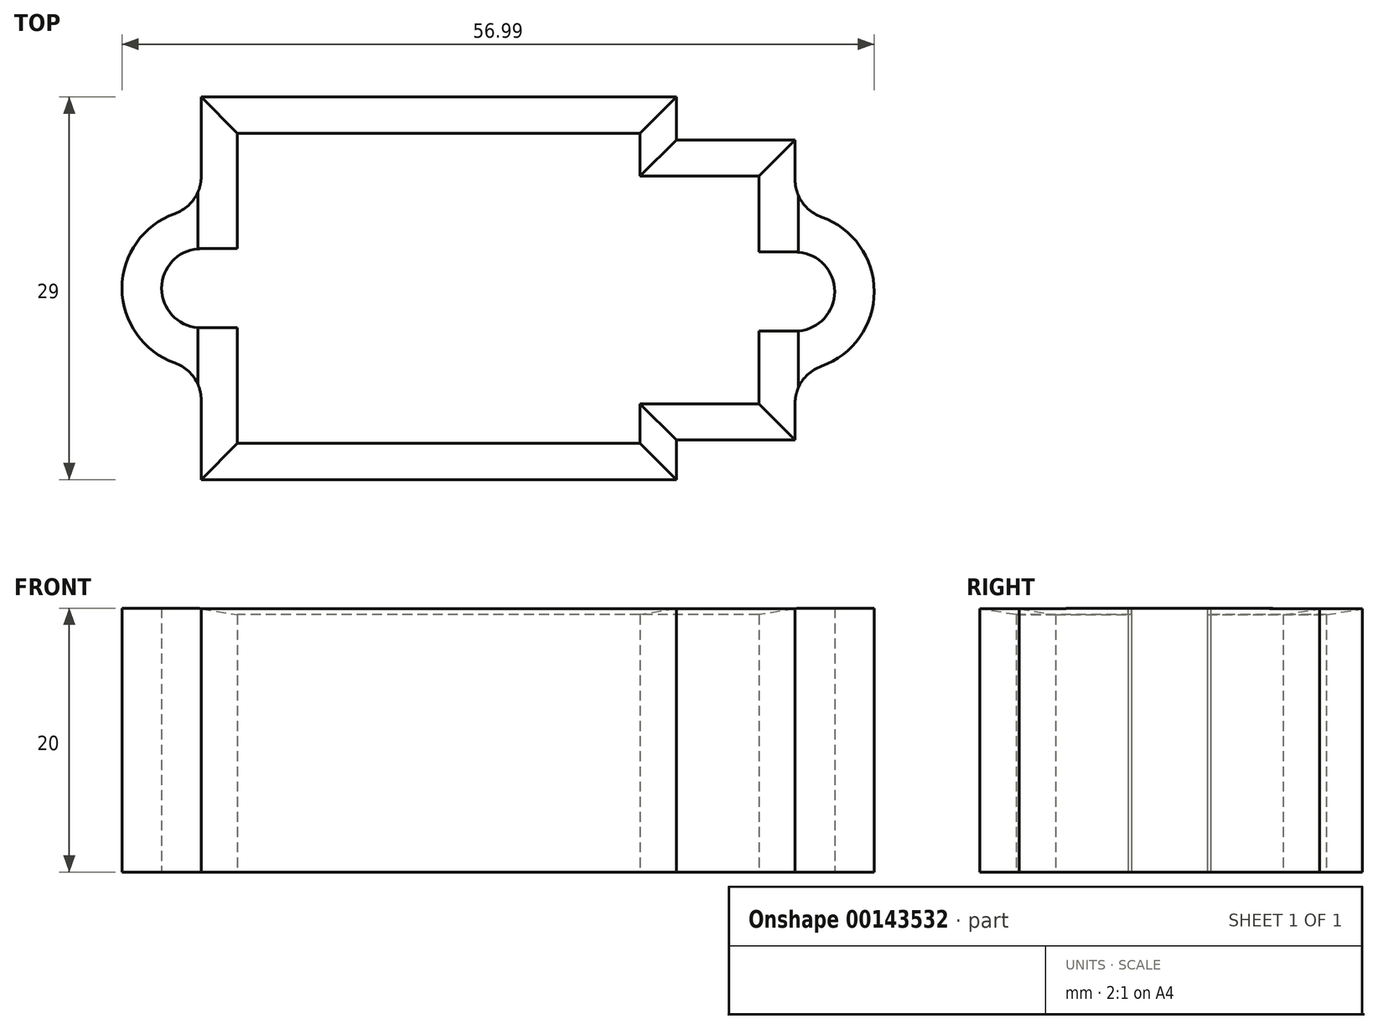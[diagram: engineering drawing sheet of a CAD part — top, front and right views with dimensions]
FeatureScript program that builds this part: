
annotation { "Feature Type Name" : "Feature", "Feature Type Description" : "" }
export const myFeature = defineFeature(function(context is Context, id is Id, definition is map)
    precondition{}
    {
        {
            var Q0;
            Q0=qCreatedBy(makeId("Top.planeOp"),FACE);
            var sketch = newSketch(context, id + "F0", { "sketchPlane" : qUnion([Q0])});
            skLineSegment(sketch, "E0.0", {"start": v(-18.12, 14.5) * mm, "end": v(17.88, 14.5) * mm});
            skLineSegment(sketch, "E1.0", {"start": v(-18.12, 14.5) * mm, "end": v(-18.12, 6) * mm});
            skLineSegment(sketch, "E2.0", {"start": v(-18.12, -14.5) * mm, "end": v(17.88, -14.5) * mm});
            skLineSegment(sketch, "E3.0", {"start": v(17.88, 14.5) * mm, "end": v(17.88, 11.25) * mm});
            skLineSegment(sketch, "E4.0", {"start": v(26.88, 11.25) * mm, "end": v(26.88, 5.74) * mm});
            skLineSegment(sketch, "E5.0", {"start": v(26.88, -11.5) * mm, "end": v(17.88, -11.5) * mm});
            skLineSegment(sketch, "E6.0", {"start": v(17.88, 11.25) * mm, "end": v(26.87, 11.25) * mm});
            skLineSegment(sketch, "E7", {"start": v(26.88, -6.24) * mm, "end": v(26.88, -11.5) * mm});
            skArc(sketch, "E8.0", {"start": v(-18.12, 6) * mm, "mid": v(-24.12, 0) * mm, "end": v(-18.12, -6) * mm});
            skLineSegment(sketch, "E9", {"start": v(-18.12, -6) * mm, "end": v(-18.12, -14.5) * mm});
            skLineSegment(sketch, "E10", {"start": v(17.88, -11.5) * mm, "end": v(17.88, -14.5) * mm});
            skLineSegment(sketch, "E11.0", {"start": v(-15.38, 11.75) * mm, "end": v(-15.38, 3) * mm});
            skLineSegment(sketch, "E12.0", {"start": v(-15.38, 11.75) * mm, "end": v(15.12, 11.75) * mm});
            skLineSegment(sketch, "E13.0", {"start": v(15.12, 8.5) * mm, "end": v(24.12, 8.5) * mm});
            skLineSegment(sketch, "E14.0", {"start": v(24.12, 8.5) * mm, "end": v(24.12, 2.75) * mm});
            skLineSegment(sketch, "E15.0", {"start": v(15.12, 11.75) * mm, "end": v(15.12, 8.5) * mm});
            skLineSegment(sketch, "E16.0", {"start": v(-15.38, -3) * mm, "end": v(-15.38, -11.75) * mm});
            skLineSegment(sketch, "E17.0", {"start": v(-15.38, -11.75) * mm, "end": v(15.12, -11.75) * mm});
            skLineSegment(sketch, "E18.0", {"start": v(15.12, -8.75) * mm, "end": v(15.12, -11.75) * mm});
            skLineSegment(sketch, "E19.0", {"start": v(24.12, -8.75) * mm, "end": v(15.12, -8.75) * mm});
            skLineSegment(sketch, "E20.0", {"start": v(24.12, -3.25) * mm, "end": v(24.12, -8.75) * mm});
            skLineSegment(sketch, "E21.0", {"start": v(-18.12, 3) * mm, "end": v(-15.38, 3) * mm});
            skLineSegment(sketch, "E22.0", {"start": v(-18.12, -3) * mm, "end": v(-15.38, -3) * mm});
            skLineSegment(sketch, "E23.0", {"start": v(24.12, -3.25) * mm, "end": v(26.88, -3.25) * mm});
            skLineSegment(sketch, "E24.0", {"start": v(26.88, 2.75) * mm, "end": v(24.12, 2.75) * mm});
            skArc(sketch, "E25", {"start": v(-18.12, -3) * mm, "mid": v(-21.12, 0) * mm, "end": v(-18.12, 3) * mm});
            skArc(sketch, "E26", {"start": v(26.88, 2.75) * mm, "mid": v(29.88, -0.25) * mm, "end": v(26.88, -3.25) * mm});
            skArc(sketch, "E27", {"start": v(26.88, 5.74) * mm, "mid": v(32.87, -0.25) * mm, "end": v(26.88, -6.24) * mm});
            skSolve(sketch);
        }
        {
            var Q0;
            Q0 = qSketchRegion(id + "F0", true);
            extrude(context, id + "F1", {"entities" : qUnion([Q0]), "depth" : 20 * mm});
        }
        {
            var Q0;
            Q0=makeQuery(id+"F1.opExtrude","SWEPT_EDGE",EDGE,{"disambiguationData":[OSD([sQuery(id+"F0.wireOp",EDGE,"E7"),sQuery(id+"F0.wireOp",EDGE,"E27")])]});
            var Q1;
            Q1=makeQuery(id+"F1.opExtrude","SWEPT_EDGE",EDGE,{"disambiguationData":[OSD([sQuery(id+"F0.wireOp",EDGE,"E4.0"),sQuery(id+"F0.wireOp",EDGE,"E27")])]});
            var Q2;
            Q2=makeQuery(id+"F1.opExtrude","SWEPT_EDGE",EDGE,{"disambiguationData":[OSD([sQuery(id+"F0.wireOp",EDGE,"E1.0"),sQuery(id+"F0.wireOp",EDGE,"E8.0")])]});
            var Q3;
            Q3=makeQuery(id+"F1.opExtrude","SWEPT_EDGE",EDGE,{"disambiguationData":[OSD([sQuery(id+"F0.wireOp",EDGE,"E8.0"),sQuery(id+"F0.wireOp",EDGE,"E9")])]});
            fillet(context, id + "F2", {"entities" : qUnion([Q0, Q1, Q2, Q3]), "radius" : 3 * mm, "tangentPropagation" : true, "allowEdgeOverflow" : false});
        }
        {
            var Q0;
            Q0=makeQuery(id+"F1.opExtrude","CAP_EDGE",EDGE,{"disambiguationData":[OSD([sQuery(id+"F0.wireOp",EDGE,"E11.0")])],"isStart":false});
            var Q1;
            Q1=makeQuery(id+"F1.opExtrude","CAP_EDGE",EDGE,{"disambiguationData":[OSD([sQuery(id+"F0.wireOp",EDGE,"E12.0")])],"isStart":false});
            var Q2;
            Q2=makeQuery(id+"F1.opExtrude","CAP_EDGE",EDGE,{"disambiguationData":[OSD([sQuery(id+"F0.wireOp",EDGE,"E16.0")])],"isStart":false});
            var Q3;
            Q3=makeQuery(id+"F1.opExtrude","CAP_EDGE",EDGE,{"disambiguationData":[OSD([sQuery(id+"F0.wireOp",EDGE,"E17.0")])],"isStart":false});
            var Q4;
            Q4=makeQuery(id+"F1.opExtrude","CAP_EDGE",EDGE,{"disambiguationData":[OSD([sQuery(id+"F0.wireOp",EDGE,"E18.0")])],"isStart":false});
            var Q5;
            Q5=makeQuery(id+"F1.opExtrude","CAP_EDGE",EDGE,{"disambiguationData":[OSD([sQuery(id+"F0.wireOp",EDGE,"E15.0")])],"isStart":false});
            var Q6;
            Q6=makeQuery(id+"F1.opExtrude","CAP_EDGE",EDGE,{"disambiguationData":[OSD([sQuery(id+"F0.wireOp",EDGE,"E13.0")])],"isStart":false});
            var Q7;
            Q7=makeQuery(id+"F1.opExtrude","CAP_EDGE",EDGE,{"disambiguationData":[OSD([sQuery(id+"F0.wireOp",EDGE,"E14.0")])],"isStart":false});
            var Q8;
            Q8=makeQuery(id+"F1.opExtrude","CAP_EDGE",EDGE,{"disambiguationData":[OSD([sQuery(id+"F0.wireOp",EDGE,"E20.0")])],"isStart":false});
            var Q9;
            Q9=makeQuery(id+"F1.opExtrude","CAP_EDGE",EDGE,{"disambiguationData":[OSD([sQuery(id+"F0.wireOp",EDGE,"E19.0")])],"isStart":false});
            chamfer(context, id + "F3", {"entities" : qUnion([Q0, Q1, Q2, Q3, Q4, Q5, Q6, Q7, Q8, Q9]), "chamferType" : ChamferType.TWO_OFFSETS, "width1" : .5 * mm, "oppositeDirection" : true, "width2" : 3 * mm, "tangentPropagation" : true});
        }
    });
